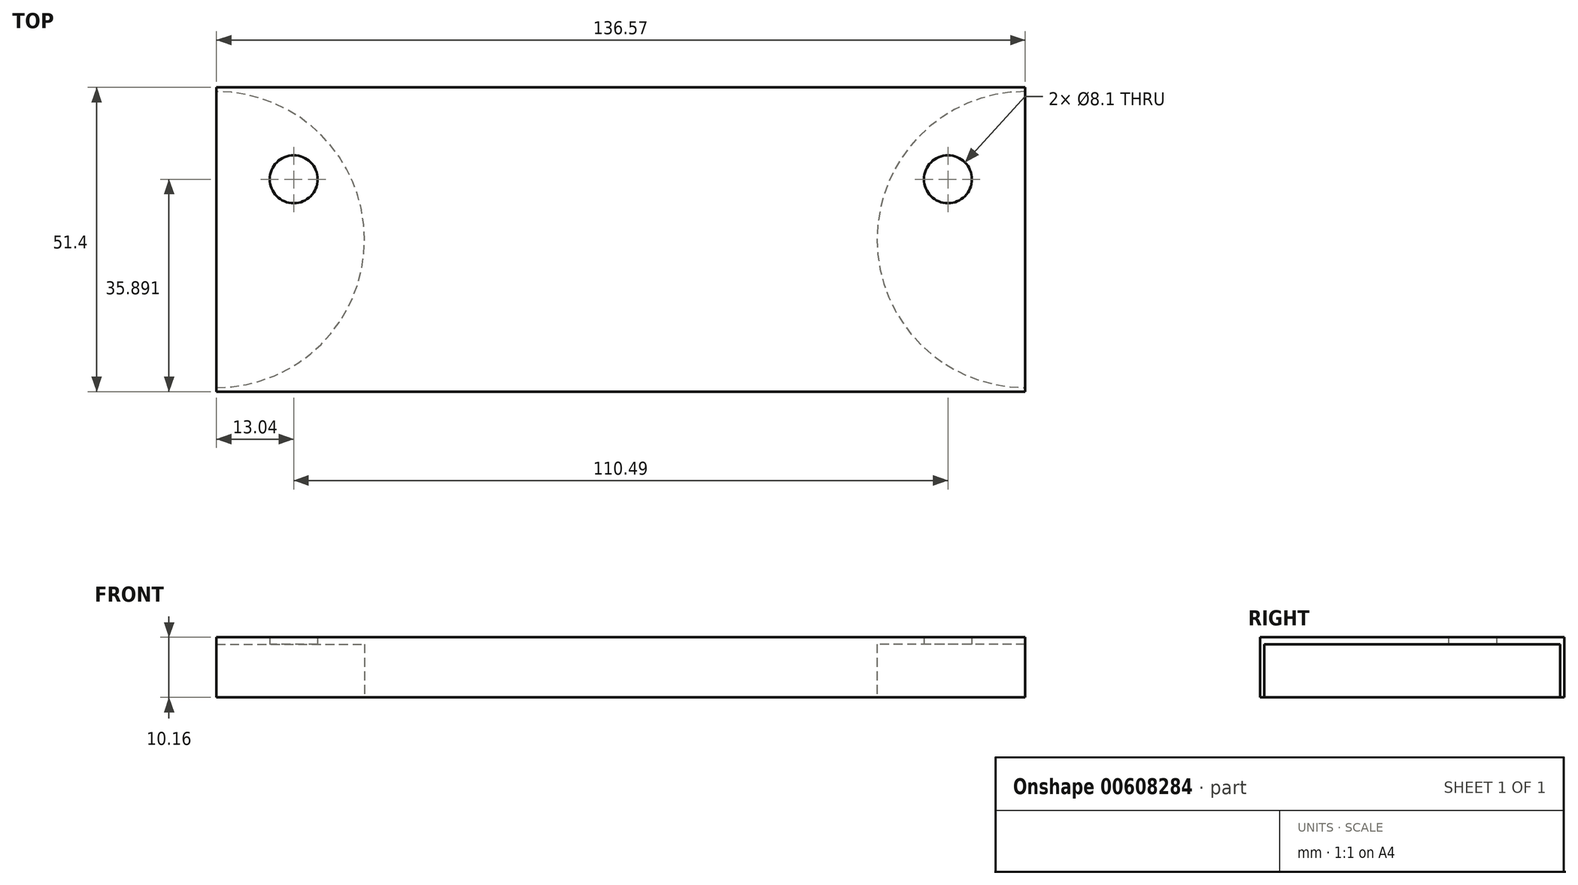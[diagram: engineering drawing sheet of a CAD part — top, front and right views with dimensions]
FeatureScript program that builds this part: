
annotation { "Feature Type Name" : "Feature", "Feature Type Description" : "" }
export const myFeature = defineFeature(function(context is Context, id is Id, definition is map)
    precondition{}
    {
        {
            var Q0;
            Q0=qCreatedBy(makeId("Top.planeOp"),FACE);
            var sketch = newSketch(context, id + "F0", { "sketchPlane" : qUnion([Q0])});
            skCircle(sketch, "E0", {"center": v(0, 0) * mm, "radius": 25.7 * mm});
            skCircle(sketch, "E1", {"center": v(13.04, 10.2) * mm, "radius": 4.05 * mm});
            skLineSegment(sketch, "E2", {"start": v(16.23, 12.69) * mm, "end": v(20.25, 15.83) * mm, "construction": true});
            skCircle(sketch, "E3", {"center": v(136.57, 0) * mm, "radius": 25.7 * mm});
            skCircle(sketch, "E4", {"center": v(123.53, 10.2) * mm, "radius": 4.05 * mm});
            skLineSegment(sketch, "E5", {"start": v(120.34, 12.69) * mm, "end": v(116.32, 15.83) * mm, "construction": true});
            skLineSegment(sketch, "E6", {"start": v(17.1, 10.2) * mm, "end": v(119.48, 10.2) * mm, "construction": true});
            skLineSegment(sketch, "E7", {"start": v(25.7, 0) * mm, "end": v(110.87, 0) * mm, "construction": true});
            skCircle(sketch, "E8", {"center": v(0, 0) * mm, "radius": 25 * mm});
            skCircle(sketch, "E9", {"center": v(136.57, 0) * mm, "radius": 25 * mm});
            skSolve(sketch);
        }
        {
            var Q0;
            Q0=makeQuery(id+"F0.imprint","IMPRINT",FACE,{"disambiguationData":[TD([[makeQuery(id+"F0.imprint","IMPRINT",EDGE,{"derivedFrom":sQuery(id+"F0.wireOp",EDGE,"E0")}),1.0]])]});
            var Q1;
            Q1=makeQuery(id+"F0.imprint","IMPRINT",FACE,{"disambiguationData":[TD([[makeQuery(id+"F0.imprint","IMPRINT",EDGE,{"derivedFrom":sQuery(id+"F0.wireOp",EDGE,"E1")}),-1.0]])]});
            var Q2;
            Q2=makeQuery(id+"F0.imprint","IMPRINT",FACE,{"disambiguationData":[TD([[makeQuery(id+"F0.imprint","IMPRINT",EDGE,{"derivedFrom":sQuery(id+"F0.wireOp",EDGE,"E3")}),1.0]])]});
            var Q3;
            Q3=makeQuery(id+"F0.imprint","IMPRINT",FACE,{"disambiguationData":[TD([[makeQuery(id+"F0.imprint","IMPRINT",EDGE,{"derivedFrom":sQuery(id+"F0.wireOp",EDGE,"E4")}),-1.0]])]});
            extrude(context, id + "F1", {"entities" : qUnion([Q0, Q1, Q2, Q3]), "depth" : 9.16 * mm, "offsetDistance" : 25 * mm});
        }
        {
            var Q0;
            Q0=qCreatedBy(makeId("Top.planeOp"),FACE);
            var sketch = newSketch(context, id + "F2", { "sketchPlane" : qUnion([Q0])});
            skCircle(sketch, "E10", {"center": v(13.04, 10.2) * mm, "radius": 4.05 * mm});
            skLineSegment(sketch, "E11", {"start": v(16.23, 12.69) * mm, "end": v(20.25, 15.83) * mm, "construction": true});
            skCircle(sketch, "E12", {"center": v(123.53, 10.2) * mm, "radius": 4.05 * mm});
            skLineSegment(sketch, "E13", {"start": v(120.34, 12.69) * mm, "end": v(116.32, 15.83) * mm, "construction": true});
            skLineSegment(sketch, "E14", {"start": v(17.1, 10.2) * mm, "end": v(119.48, 10.2) * mm, "construction": true});
            skCircle(sketch, "E15", {"center": v(0, 0) * mm, "radius": 25 * mm});
            skCircle(sketch, "E16", {"center": v(136.57, 0) * mm, "radius": 25 * mm});
            skSolve(sketch);
        }
        {
            var Q0;
            Q0=qCreatedBy(makeId("Top.planeOp"),FACE);
            var sketch = newSketch(context, id + "F3", { "sketchPlane" : qUnion([Q0])});
            skLineSegment(sketch, "E17.bottom", {"start": v(0, 25.7) * mm, "end": v(136.57, 25.7) * mm});
            skLineSegment(sketch, "E17.top", {"start": v(0, -25.7) * mm, "end": v(136.57, -25.7) * mm});
            skLineSegment(sketch, "E17.left", {"start": v(0, 25.7) * mm, "end": v(0, -25.7) * mm});
            skLineSegment(sketch, "E17.right", {"start": v(136.57, 25.7) * mm, "end": v(136.57, -25.7) * mm});
            skPoint(sketch, "E18.endSnap0", {"position": v(136.57, 0) * mm});
            skLineSegment(sketch, "E19", {"start": v(162.27, 0) * mm, "end": v(110.87, 0) * mm, "construction": true});
            skSolve(sketch);
        }
        {
            var Q0;
            Q0 = qSketchRegion(id + "F3", true);
            extrude(context, id + "F4", {"entities" : qUnion([Q0]), "operationType" : NewBodyOperationType.ADD, "depth" : 9.16 * mm, "offsetDistance" : 25 * mm});
        }
        {
            var Q0;
            Q0 = qSketchRegion(id + "F2", true);
            extrude(context, id + "F5", {"entities" : qUnion([Q0]), "operationType" : NewBodyOperationType.REMOVE, "depth" : 9 * mm, "offsetDistance" : 25 * mm});
        }
        {
            var Q0;
            Q0=makeQuery(id+"F5.boolean.opBoolean","SPLIT",FACE,{"disambiguationData":[TD([makeQuery(id+"F5.opExtrude","SWEPT_FACE",FACE,{"disambiguationData":[OSD([sQuery(id+"F2.wireOp",EDGE,"E12")])]})])],"derivedFrom":makeQuery(id+"F4.boolean.opBoolean","MERGE",FACE,{"derivedFrom":[makeQuery(id+"F1.opExtrude","CAP_FACE",FACE,{"disambiguationData":[OSD([sQuery(id+"F0.wireOp",EDGE,"E0"),sQuery(id+"F0.wireOp",EDGE,"E1")])],"isStart":true}),makeQuery(id+"F1.opExtrude","CAP_FACE",FACE,{"disambiguationData":[OSD([sQuery(id+"F0.wireOp",EDGE,"E3"),sQuery(id+"F0.wireOp",EDGE,"E4")])],"isStart":true}),makeQuery(id+"F4.opExtrude","CAP_FACE",FACE,{"disambiguationData":[OSD([sQuery(id+"F3.wireOp",EDGE,"E17.bottom"),sQuery(id+"F3.wireOp",EDGE,"E17.top"),sQuery(id+"F3.wireOp",EDGE,"E17.left"),sQuery(id+"F3.wireOp",EDGE,"E17.right")])],"isStart":true})]})});
            var Q1;
            Q1=makeQuery(id+"F5.boolean.opBoolean","SPLIT",FACE,{"disambiguationData":[TD([makeQuery(id+"F5.opExtrude","SWEPT_FACE",FACE,{"disambiguationData":[OSD([sQuery(id+"F2.wireOp",EDGE,"E10")])]})])],"derivedFrom":makeQuery(id+"F4.boolean.opBoolean","MERGE",FACE,{"derivedFrom":[makeQuery(id+"F1.opExtrude","CAP_FACE",FACE,{"disambiguationData":[OSD([sQuery(id+"F0.wireOp",EDGE,"E0"),sQuery(id+"F0.wireOp",EDGE,"E1")])],"isStart":true}),makeQuery(id+"F1.opExtrude","CAP_FACE",FACE,{"disambiguationData":[OSD([sQuery(id+"F0.wireOp",EDGE,"E3"),sQuery(id+"F0.wireOp",EDGE,"E4")])],"isStart":true}),makeQuery(id+"F4.opExtrude","CAP_FACE",FACE,{"disambiguationData":[OSD([sQuery(id+"F3.wireOp",EDGE,"E17.bottom"),sQuery(id+"F3.wireOp",EDGE,"E17.top"),sQuery(id+"F3.wireOp",EDGE,"E17.left"),sQuery(id+"F3.wireOp",EDGE,"E17.right")])],"isStart":true})]})});
            var Q2;
            Q2=sQuery(id+"F2.wireOp",EDGE,"E12");
            var Q3;
            Q3=sQuery(id+"F2.wireOp",EDGE,"E10");
            extrude(context, id + "F6", {"entities" : qUnion([Q0, Q1]), "operationType" : NewBodyOperationType.REMOVE, "surfaceEntities" : qUnion([Q2, Q3]), "oppositeDirection" : true, "depth" : 25 * mm, "offsetDistance" : 25 * mm});
        }
        {
            var Q0;
            Q0=qCreatedBy(makeId("Top.planeOp"),FACE);
            var sketch = newSketch(context, id + "F7", { "sketchPlane" : qUnion([Q0])});
            skLineSegment(sketch, "E20.left", {"start": v(162.27, 0) * mm, "end": v(162.27, 37.04) * mm, "construction": true});
            skLineSegment(sketch, "E20.right", {"start": v(-25.7, 0) * mm, "end": v(-25.7, 37.04) * mm, "construction": true});
            skLineSegment(sketch, "E21.left", {"start": v(162.27, 0) * mm, "end": v(162.27, -37.04) * mm, "construction": true});
            skLineSegment(sketch, "E21.right", {"start": v(-25.7, 0) * mm, "end": v(-25.7, -37.04) * mm, "construction": true});
            skLineSegment(sketch, "E22.bottom", {"start": v(162.27, 37.04) * mm, "end": v(136.57, 37.04) * mm});
            skLineSegment(sketch, "E22.top", {"start": v(162.27, -37.04) * mm, "end": v(136.57, -37.04) * mm});
            skLineSegment(sketch, "E22.left", {"start": v(162.27, 37.04) * mm, "end": v(162.27, -37.04) * mm});
            skLineSegment(sketch, "E22.right", {"start": v(136.57, 37.04) * mm, "end": v(136.57, -37.04) * mm});
            skLineSegment(sketch, "E23.bottom", {"start": v(-25.7, 37.04) * mm, "end": v(0, 37.04) * mm});
            skLineSegment(sketch, "E23.top", {"start": v(-25.7, -37.04) * mm, "end": v(0, -37.04) * mm});
            skLineSegment(sketch, "E23.left", {"start": v(-25.7, 37.04) * mm, "end": v(-25.7, -37.04) * mm});
            skLineSegment(sketch, "E23.right", {"start": v(0, 37.04) * mm, "end": v(0, -37.04) * mm});
            skLineSegment(sketch, "E24", {"start": v(162.27, 0) * mm, "end": v(-25.7, 0) * mm, "construction": true});
            skLineSegment(sketch, "E25", {"start": v(136.57, -25) * mm, "end": v(136.57, 25) * mm, "construction": true});
            skPoint(sketch, "E26", {"position": v(136.57, 0) * mm});
            skSolve(sketch);
        }
        {
            var Q0;
            Q0=makeQuery(id+"F7.imprint","IMPRINT",FACE,{"disambiguationData":[TD([[makeQuery(id+"F7.imprint","IMPRINT",EDGE,{"derivedFrom":sQuery(id+"F7.wireOp",EDGE,"E23.bottom")}),-1.0]])]});
            var Q1;
            Q1=makeQuery(id+"F7.imprint","IMPRINT",FACE,{"disambiguationData":[TD([[makeQuery(id+"F7.imprint","IMPRINT",EDGE,{"derivedFrom":sQuery(id+"F7.wireOp",EDGE,"E22.bottom")}),1.0]])]});
            extrude(context, id + "F8", {"entities" : qUnion([Q0, Q1]), "operationType" : NewBodyOperationType.REMOVE, "depth" : 25 * mm, "offsetDistance" : 25 * mm});
        }
        {
            var Q0;
            Q0=makeQuery(id+"F4.boolean.opBoolean","MERGE",FACE,{"derivedFrom":[makeQuery(id+"F1.opExtrude","CAP_FACE",FACE,{"disambiguationData":[OSD([sQuery(id+"F0.wireOp",EDGE,"E0"),sQuery(id+"F0.wireOp",EDGE,"E1")])],"isStart":false}),makeQuery(id+"F1.opExtrude","CAP_FACE",FACE,{"disambiguationData":[OSD([sQuery(id+"F0.wireOp",EDGE,"E3"),sQuery(id+"F0.wireOp",EDGE,"E4")])],"isStart":false}),makeQuery(id+"F4.opExtrude","CAP_FACE",FACE,{"disambiguationData":[OSD([sQuery(id+"F3.wireOp",EDGE,"E17.bottom"),sQuery(id+"F3.wireOp",EDGE,"E17.top"),sQuery(id+"F3.wireOp",EDGE,"E17.left"),sQuery(id+"F3.wireOp",EDGE,"E17.right")])],"isStart":false})]});
            extrude(context, id + "F9", {"entities" : qUnion([Q0]), "operationType" : NewBodyOperationType.ADD, "depth" : 1 * mm, "offsetDistance" : 25 * mm});
        }
    });
